# Revit family: turia_l_672416_002_07_79a2
name_source: partatom
category: Lighting Fixtures
units: mm (PartAtom-declared; Revit-internal decimal feet)

## family parameters
Cut with Voids When Loaded = No
Host = Face
Light Source = No
Part Type = Normal
Room Calculation Point = No
Round Connector Dimension = Use Diameter
Shared = No

## types (1)
- TURIA L (1 x LED Modul 765, 270 lm, 6500)
    Apparent Load = 5 VA
    CIE Flux Codes = 35 68 98 100 100
    Color Rendering = 70
    Color Temperature = 6500
    Default Elevation = 1800 mm
    Description = Series: TURIA L
Round emergency luminaire for escape route lighting. Housing: die-cast aluminium. Bezel ring: plastic. With plastic lenses for escape route illumination. Self-contained system with automatic self-test and feedback via DALI bus, only to RZB DALI monitoring system. With enclosed separate ceiling mounting ring also suitable for ceiling cut-outs of Ø 68 mm. 
Colour: white
Diameter: 62 mm
Height: 3 mm
Cut-out diameter: 54-68 mm
Recess height: 76-162 mm
Luminaire: recess height: 42 mm
Weight: 550 g
Operating mode: non-maintained power mode
Duration time: 8 h
Lamp: LED
Socket: without socket
Colour temperature: 6500K
Colour rendering index (CRI): 70
System power: 5.2 W
Rated luminous flux: 270 lm
Luminous flux, emergency: 130 lm
System power, emergency: -
Control gear: Regulated power supply
Protection class: II
Type of protection: IP 20
    Height = 0 mm  [stored 0 ft]
    Lamp = 1 x LED Modul 765
    Lamp Light Flux = 270 lm
    Lamp count = 1
    Length = 62 mm  [stored 0.203412 ft]
    Lifetime = 50000 h
    Luminous efficacy = 52 lm/W
    Manufacturer = RZB
    ModVariant = No
    Model = 672416.002.07
    Mounting Place = Ceiling
    Mounting Type = Recessed
    Number of Poles = 1
    OnlyDefault = Yes
    Power Factor = 1
    Product Name = TURIA L
    Product group = Recessed ceiling luminaires
    ProductGroupID = 405
    Protection Class = Protection class II
    Protection Degree = IP 20
    RLX_Detail_Level = 1
    RLX_Emergency_Light_Flux = 130 lm
    RLX_Emergency_Type = 3
    RLX_Emergency_Type_DB = Yes
    RlxData = <blob elided: 44621 chars, md5=8039cc5a>
    Socket = socket
    Standby Power = 0 W
    System Light Flux = 270 lm
    System Power = 5 W
    Type Comments = Product without accessories
    Type Image = 672414.002.jpg
    URL = http://relux.com
    VarID = ---
    Voltage = 230 V
    Voltage Range = 220-240 V
    Weight = 0.00 kg
    Width = 0 mm  [stored 0 ft]

note: [stored X ft] marks values corroborated as IEEE doubles in the binary element streams (Revit-internal decimal feet)

## geometry (parser evidence)
native form markers: Sweep x10
no freeform markers — native parametric forms only
